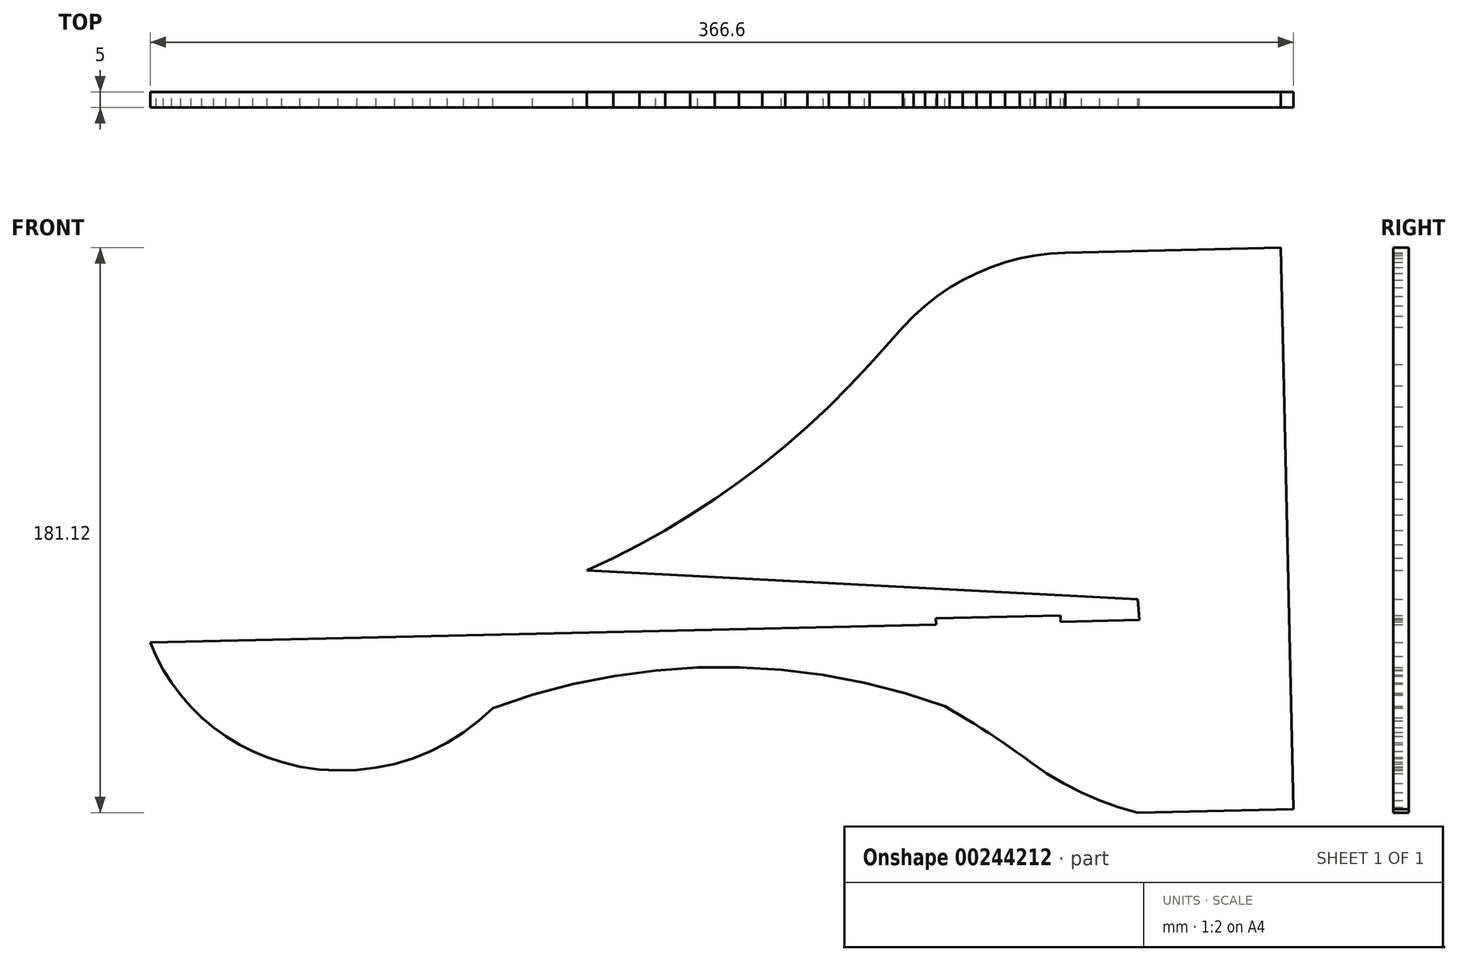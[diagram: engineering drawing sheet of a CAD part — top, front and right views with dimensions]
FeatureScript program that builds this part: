
annotation { "Feature Type Name" : "Feature", "Feature Type Description" : "" }
export const myFeature = defineFeature(function(context is Context, id is Id, definition is map)
    precondition{}
    {
        {
            var Q0;
            Q0=qCreatedBy(makeId("Front.planeOp"),FACE);
            var sketch = newSketch(context, id + "F0", { "sketchPlane" : qUnion([Q0])});
            skLineSegment(sketch, "E0", {"start": v(104.2, -77.98) * mm, "end": v(98.95, -74.36) * mm});
            skLineSegment(sketch, "E1", {"start": v(98.95, -74.36) * mm, "end": v(96.75, -72.75) * mm});
            skLineSegment(sketch, "E2", {"start": v(96.75, -72.75) * mm, "end": v(94.53, -71.16) * mm});
            skLineSegment(sketch, "E3", {"start": v(94.53, -71.16) * mm, "end": v(92.29, -69.59) * mm});
            skLineSegment(sketch, "E4", {"start": v(92.29, -69.59) * mm, "end": v(90.04, -68.04) * mm});
            skLineSegment(sketch, "E5", {"start": v(90.04, -68.04) * mm, "end": v(87.77, -66.5) * mm});
            skLineSegment(sketch, "E6", {"start": v(87.77, -66.5) * mm, "end": v(85.49, -65) * mm});
            skLineSegment(sketch, "E7", {"start": v(85.49, -65) * mm, "end": v(83.2, -63.52) * mm});
            skLineSegment(sketch, "E8", {"start": v(83.2, -63.52) * mm, "end": v(80.88, -62.06) * mm});
            skLineSegment(sketch, "E9", {"start": v(80.88, -62.06) * mm, "end": v(78.56, -60.62) * mm});
            skLineSegment(sketch, "E10", {"start": v(78.56, -60.62) * mm, "end": v(76.22, -59.2) * mm});
            skLineSegment(sketch, "E11", {"start": v(76.22, -59.2) * mm, "end": v(73.87, -57.8) * mm});
            skLineSegment(sketch, "E12", {"start": v(73.87, -57.8) * mm, "end": v(71.5, -56.43) * mm});
            skLineSegment(sketch, "E13", {"start": v(71.5, -56.43) * mm, "end": v(58.72, -52.28) * mm});
            skLineSegment(sketch, "E14", {"start": v(58.72, -52.28) * mm, "end": v(45.69, -48.94) * mm});
            skLineSegment(sketch, "E15", {"start": v(45.69, -48.94) * mm, "end": v(32.47, -46.45) * mm});
            skLineSegment(sketch, "E16", {"start": v(32.47, -46.45) * mm, "end": v(19.13, -44.8) * mm});
            skLineSegment(sketch, "E17", {"start": v(19.13, -44.8) * mm, "end": v(5.7, -44) * mm});
            skLineSegment(sketch, "E18", {"start": v(5.7, -44) * mm, "end": v(-7.75, -44.06) * mm});
            skLineSegment(sketch, "E19", {"start": v(-7.75, -44.06) * mm, "end": v(-21.16, -44.97) * mm});
            skLineSegment(sketch, "E20", {"start": v(-21.16, -44.97) * mm, "end": v(-34.5, -46.74) * mm});
            skLineSegment(sketch, "E21", {"start": v(-34.5, -46.74) * mm, "end": v(-47.69, -49.36) * mm});
            skLineSegment(sketch, "E22", {"start": v(-47.69, -49.36) * mm, "end": v(-60.69, -52.8) * mm});
            skLineSegment(sketch, "E23", {"start": v(-60.69, -52.8) * mm, "end": v(-73.44, -57.07) * mm});
            skLineSegment(sketch, "E24", {"start": v(-73.44, -57.07) * mm, "end": v(-77.96, -61.17) * mm});
            skLineSegment(sketch, "E25", {"start": v(-77.96, -61.17) * mm, "end": v(-82.82, -64.86) * mm});
            skLineSegment(sketch, "E26", {"start": v(-82.82, -64.86) * mm, "end": v(-87.99, -68.1) * mm});
            skLineSegment(sketch, "E27", {"start": v(-87.99, -68.1) * mm, "end": v(-93.42, -70.88) * mm});
            skLineSegment(sketch, "E28", {"start": v(-93.42, -70.88) * mm, "end": v(-99.08, -73.16) * mm});
            skLineSegment(sketch, "E29", {"start": v(-99.08, -73.16) * mm, "end": v(-104.92, -74.94) * mm});
            skLineSegment(sketch, "E30", {"start": v(-104.92, -74.94) * mm, "end": v(-110.9, -76.19) * mm});
            skLineSegment(sketch, "E31", {"start": v(-110.9, -76.19) * mm, "end": v(-116.95, -76.9) * mm});
            skLineSegment(sketch, "E32", {"start": v(-116.95, -76.9) * mm, "end": v(-123.05, -77.08) * mm});
            skLineSegment(sketch, "E33", {"start": v(-123.05, -77.08) * mm, "end": v(-129.14, -76.72) * mm});
            skLineSegment(sketch, "E34", {"start": v(-129.14, -76.72) * mm, "end": v(-135.18, -75.82) * mm});
            skLineSegment(sketch, "E35", {"start": v(-135.18, -75.82) * mm, "end": v(-141.1, -74.4) * mm});
            skLineSegment(sketch, "E36", {"start": v(-141.1, -74.4) * mm, "end": v(-145.78, -72.85) * mm});
            skLineSegment(sketch, "E37", {"start": v(-145.78, -72.85) * mm, "end": v(-150.33, -70.95) * mm});
            skLineSegment(sketch, "E38", {"start": v(-150.33, -70.95) * mm, "end": v(-154.72, -68.72) * mm});
            skLineSegment(sketch, "E39", {"start": v(-154.72, -68.72) * mm, "end": v(-158.92, -66.15) * mm});
            skLineSegment(sketch, "E40", {"start": v(-158.92, -66.15) * mm, "end": v(-162.91, -63.27) * mm});
            skLineSegment(sketch, "E41", {"start": v(-162.91, -63.27) * mm, "end": v(-166.68, -60.1) * mm});
            skLineSegment(sketch, "E42", {"start": v(-166.68, -60.1) * mm, "end": v(-170.2, -56.65) * mm});
            skLineSegment(sketch, "E43", {"start": v(-170.2, -56.65) * mm, "end": v(-173.43, -52.94) * mm});
            skLineSegment(sketch, "E44", {"start": v(-173.43, -52.94) * mm, "end": v(-176.38, -49) * mm});
            skLineSegment(sketch, "E45", {"start": v(-176.38, -49) * mm, "end": v(-179.01, -44.84) * mm});
            skLineSegment(sketch, "E46", {"start": v(-179.01, -44.84) * mm, "end": v(-181.33, -40.5) * mm});
            skLineSegment(sketch, "E47", {"start": v(-181.33, -40.5) * mm, "end": v(-183.3, -35.98) * mm});
            skLineSegment(sketch, "E48", {"start": v(-183.3, -35.98) * mm, "end": v(13.69, -31.51) * mm});
            skLineSegment(sketch, "E49", {"start": v(13.69, -31.51) * mm, "end": v(68.67, -30.26) * mm});
            skLineSegment(sketch, "E50", {"start": v(68.67, -30.26) * mm, "end": v(68.63, -28.26) * mm});
            skLineSegment(sketch, "E51", {"start": v(68.63, -28.26) * mm, "end": v(108.62, -27.36) * mm});
            skLineSegment(sketch, "E52", {"start": v(108.62, -27.36) * mm, "end": v(108.66, -29.36) * mm});
            skLineSegment(sketch, "E53", {"start": v(108.66, -29.36) * mm, "end": v(133.85, -28.79) * mm});
            skLineSegment(sketch, "E54", {"start": v(133.85, -28.79) * mm, "end": v(133.4, -22.16) * mm});
            skLineSegment(sketch, "E55", {"start": v(133.4, -22.16) * mm, "end": v(-43.26, -12.9) * mm});
            skLineSegment(sketch, "E56", {"start": v(-43.26, -12.9) * mm, "end": v(-34.74, -8.9) * mm});
            skLineSegment(sketch, "E57", {"start": v(-34.74, -8.9) * mm, "end": v(-26.37, -4.6) * mm});
            skLineSegment(sketch, "E58", {"start": v(-26.37, -4.6) * mm, "end": v(-18.14, -0.02) * mm});
            skLineSegment(sketch, "E59", {"start": v(-18.14, -0.02) * mm, "end": v(-10.08, 4.84) * mm});
            skLineSegment(sketch, "E60", {"start": v(-10.08, 4.84) * mm, "end": v(-2.2, 9.98) * mm});
            skLineSegment(sketch, "E61", {"start": v(-2.2, 9.98) * mm, "end": v(5.5, 15.4) * mm});
            skLineSegment(sketch, "E62", {"start": v(5.5, 15.4) * mm, "end": v(13.01, 21.07) * mm});
            skLineSegment(sketch, "E63", {"start": v(13.01, 21.07) * mm, "end": v(20.32, 27) * mm});
            skLineSegment(sketch, "E64", {"start": v(20.32, 27) * mm, "end": v(27.42, 33.2) * mm});
            skLineSegment(sketch, "E65", {"start": v(27.42, 33.2) * mm, "end": v(34.3, 39.62) * mm});
            skLineSegment(sketch, "E66", {"start": v(34.3, 39.62) * mm, "end": v(40.95, 46.28) * mm});
            skLineSegment(sketch, "E67", {"start": v(40.95, 46.28) * mm, "end": v(47.36, 53.17) * mm});
            skLineSegment(sketch, "E68", {"start": v(47.36, 53.17) * mm, "end": v(58.08, 65.08) * mm});
            skLineSegment(sketch, "E69", {"start": v(58.08, 65.08) * mm, "end": v(61.49, 68.62) * mm});
            skLineSegment(sketch, "E70", {"start": v(61.49, 68.62) * mm, "end": v(65.13, 71.91) * mm});
            skLineSegment(sketch, "E71", {"start": v(65.13, 71.91) * mm, "end": v(68.98, 74.96) * mm});
            skLineSegment(sketch, "E72", {"start": v(68.98, 74.96) * mm, "end": v(73.03, 77.73) * mm});
            skLineSegment(sketch, "E73", {"start": v(73.03, 77.73) * mm, "end": v(77.26, 80.22) * mm});
            skLineSegment(sketch, "E74", {"start": v(77.26, 80.22) * mm, "end": v(81.65, 82.42) * mm});
            skLineSegment(sketch, "E75", {"start": v(81.65, 82.42) * mm, "end": v(86.18, 84.32) * mm});
            skLineSegment(sketch, "E76", {"start": v(86.18, 84.32) * mm, "end": v(90.83, 85.9) * mm});
            skLineSegment(sketch, "E77", {"start": v(90.83, 85.9) * mm, "end": v(95.57, 87.17) * mm});
            skLineSegment(sketch, "E78", {"start": v(95.57, 87.17) * mm, "end": v(100.4, 88.1) * mm});
            skLineSegment(sketch, "E79", {"start": v(100.4, 88.1) * mm, "end": v(105.27, 88.72) * mm});
            skLineSegment(sketch, "E80", {"start": v(105.27, 88.72) * mm, "end": v(110.17, 89) * mm});
            skLineSegment(sketch, "E81", {"start": v(110.17, 89) * mm, "end": v(179.22, 90.56) * mm});
            skLineSegment(sketch, "E82", {"start": v(179.22, 90.56) * mm, "end": v(183.3, -89.43) * mm});
            skLineSegment(sketch, "E83", {"start": v(183.3, -89.43) * mm, "end": v(133.31, -90.56) * mm});
            skLineSegment(sketch, "E84", {"start": v(133.31, -90.56) * mm, "end": v(127.19, -88.82) * mm});
            skLineSegment(sketch, "E85", {"start": v(127.19, -88.82) * mm, "end": v(121.19, -86.67) * mm});
            skLineSegment(sketch, "E86", {"start": v(121.19, -86.67) * mm, "end": v(115.34, -84.15) * mm});
            skLineSegment(sketch, "E87", {"start": v(115.34, -84.15) * mm, "end": v(109.67, -81.24) * mm});
            skLineSegment(sketch, "E88", {"start": v(109.67, -81.24) * mm, "end": v(104.2, -77.98) * mm});
            skSolve(sketch);
        }
        {
            var Q0;
            Q0 = qSketchRegion(id + "F0", true);
            extrude(context, id + "F1", {"entities" : qUnion([Q0]), "depth" : 5 * mm});
        }
    });
